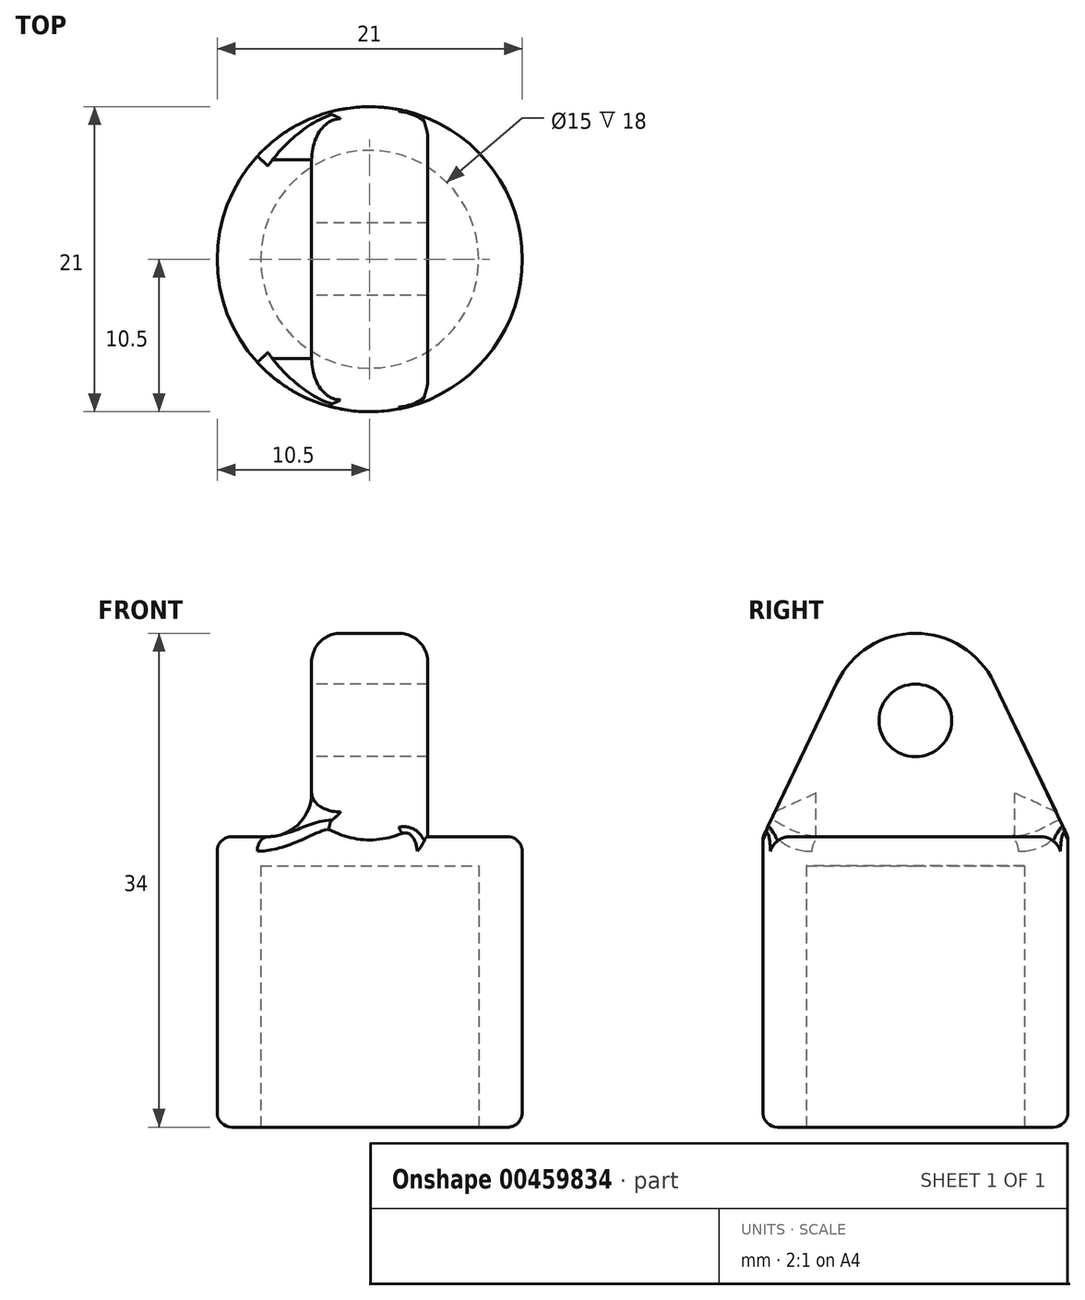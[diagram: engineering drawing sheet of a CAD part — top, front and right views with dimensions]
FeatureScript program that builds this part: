
annotation { "Feature Type Name" : "Feature", "Feature Type Description" : "" }
export const myFeature = defineFeature(function(context is Context, id is Id, definition is map)
    precondition{}
    {
        {
            var Q0;
            Q0=qCreatedBy(makeId("Front.planeOp"),FACE);
            var sketch = newSketch(context, id + "F0", { "sketchPlane" : qUnion([Q0])});
            skLineSegment(sketch, "E0", {"start": v(0, 0) * mm, "end": v(-10.5, 0) * mm});
            skLineSegment(sketch, "E1", {"start": v(-10.5, 0) * mm, "end": v(-10.5, -20) * mm});
            skLineSegment(sketch, "E2", {"start": v(-10.5, -20) * mm, "end": v(-7.5, -20) * mm});
            skLineSegment(sketch, "E3", {"start": v(-7.5, -20) * mm, "end": v(-7.5, -2) * mm});
            skLineSegment(sketch, "E4", {"start": v(-7.5, -2) * mm, "end": v(0, -2) * mm});
            skLineSegment(sketch, "E5", {"start": v(0, -2) * mm, "end": v(0, 0) * mm});
            skSolve(sketch);
        }
        {
            var Q0;
            Q0 = qSketchRegion(id + "F0", true);
            var Q1;
            Q1=sQuery(id+"F0.wireOp",EDGE,"E5");
            revolve(context, id + "F1", {"entities" : qUnion([Q0]), "axis" : qUnion([Q1]), "revolveType" : RevolveType.FULL});
        }
        {
            var Q0;
            Q0=qCreatedBy(makeId("Right.planeOp"),FACE);
            var sketch = newSketch(context, id + "F2", { "sketchPlane" : qUnion([Q0])});
            skCircle(sketch, "E6", {"center": v(0, 8) * mm, "radius": 2.5 * mm});
            skCircle(sketch, "E7", {"center": v(0, 8) * mm, "radius": 6 * mm});
            skLineSegment(sketch, "E8", {"start": v(0, 0) * mm, "end": v(-10.5, 0) * mm});
            skLineSegment(sketch, "E9", {"start": v(-10.5, 0) * mm, "end": v(-5.4, 10.6) * mm});
            skLineSegment(sketch, "E10.MirrorCS", {"start": v(10.5, 0) * mm, "end": v(5.4, 10.6) * mm});
            skLineSegment(sketch, "E11", {"start": v(10.5, 0) * mm, "end": v(0, 0) * mm});
            skSolve(sketch);
        }
        {
            var Q0;
            Q0 = qSketchRegion(id + "F2", true);
            extrude(context, id + "F3", {"entities" : qUnion([Q0]), "operationType" : NewBodyOperationType.ADD, "endBound" : BoundingType.SYMMETRIC, "depth" : 8 * mm, "offsetDistance" : 25 * mm});
        }
        {
            var Q0;
            Q0=makeQuery(id+"F1.opRevolve","SWEPT_FACE",FACE,{"disambiguationData":[OSD([sQuery(id+"F0.wireOp",EDGE,"E2")])]});
            var sketch = newSketch(context, id + "F4", { "sketchPlane" : qUnion([Q0])});
            skCircle(sketch, "E12", {"center": v(0, 0) * mm, "radius": 10.5 * mm});
            skCircle(sketch, "E13", {"center": v(0, 0) * mm, "radius": 15.5 * mm});
            skSolve(sketch);
        }
        {
            var Q0;
            Q0 = qSketchRegion(id + "F4", true);
            extrude(context, id + "F5", {"entities" : qUnion([Q0]), "operationType" : NewBodyOperationType.REMOVE, "endBound" : BoundingType.THROUGH_ALL, "oppositeDirection" : true, "depth" : 25 * mm, "offsetDistance" : 25 * mm});
        }
        {
            var Q0;
            Q0=makeQuery(id+"F3.opExtrude","CAP_EDGE",EDGE,{"disambiguationData":[OSD([sQuery(id+"F2.wireOp",EDGE,"E7")])],"isStart":false});
            var Q1;
            Q1=makeQuery(id+"F3.opExtrude","CAP_EDGE",EDGE,{"disambiguationData":[OSD([sQuery(id+"F2.wireOp",EDGE,"E7")])],"isStart":true});
            fillet(context, id + "F6", {"entities" : qUnion([Q0, Q1]), "radius" : 2 * mm, "tangentPropagation" : true, "allowEdgeOverflow" : false});
        }
        {
            var Q0;
            {var subQ0=sQuery(id+"F2.wireOp",EDGE,"E11");var subQ1=sQuery(id+"F2.wireOp",EDGE,"E8");Q0=makeQuery(id+"F3.boolean.opBoolean","SPLIT",EDGE,{"disambiguationData":[topologyDisambiguationEdgeConnected([makeQuery(id+"F1.opRevolve","SWEPT_FACE",FACE,{"disambiguationData":[OSD([sQuery(id+"F0.wireOp",EDGE,"E0")])]}),makeQuery(id+"F3.opExtrude","CAP_FACE",FACE,{"disambiguationData":[OSD([sQuery(id+"F2.wireOp",EDGE,"E6"),sQuery(id+"F2.wireOp",EDGE,"E7"),subQ1,sQuery(id+"F2.wireOp",EDGE,"E9"),sQuery(id+"F2.wireOp",EDGE,"E10.MirrorCS"),subQ0])],"isStart":false})])],"derivedFrom":makeQuery(id+"F3.opExtrude","CAP_EDGE",EDGE,{"disambiguationData":[OSD([subQ1,subQ0])],"isStart":false})});}
            var Q1;
            {var subQ0=sQuery(id+"F2.wireOp",EDGE,"E11");var subQ1=sQuery(id+"F2.wireOp",EDGE,"E8");Q1=makeQuery(id+"F3.boolean.opBoolean","SPLIT",EDGE,{"disambiguationData":[topologyDisambiguationEdgeConnected([makeQuery(id+"F1.opRevolve","SWEPT_FACE",FACE,{"disambiguationData":[OSD([sQuery(id+"F0.wireOp",EDGE,"E0")])]}),makeQuery(id+"F3.opExtrude","CAP_FACE",FACE,{"disambiguationData":[OSD([sQuery(id+"F2.wireOp",EDGE,"E6"),sQuery(id+"F2.wireOp",EDGE,"E7"),subQ1,sQuery(id+"F2.wireOp",EDGE,"E9"),sQuery(id+"F2.wireOp",EDGE,"E10.MirrorCS"),subQ0])],"isStart":true})])],"derivedFrom":makeQuery(id+"F3.opExtrude","CAP_EDGE",EDGE,{"disambiguationData":[OSD([subQ1,subQ0])],"isStart":true})});}
            fillet(context, id + "F7", {"entities" : qUnion([Q0, Q1]), "radius" : 3 * mm, "tangentPropagation" : true, "allowEdgeOverflow" : false});
        }
        {
            var Q0;
            Q0=makeQuery(id+"F5.boolean.opBoolean","MERGE",FACE,{"derivedFrom":[makeQuery(id+"F1.opRevolve","SWEPT_FACE",FACE,{"disambiguationData":[OSD([sQuery(id+"F0.wireOp",EDGE,"E1")])]}),makeQuery(id+"F5.opExtrude","SWEPT_FACE",FACE,{"disambiguationData":[OSD([sQuery(id+"F4.wireOp",EDGE,"E12")])]})]});
            fillet(context, id + "F8", {"entities" : qUnion([Q0]), "radius" : 1 * mm, "tangentPropagation" : true, "allowEdgeOverflow" : false});
        }
    });
